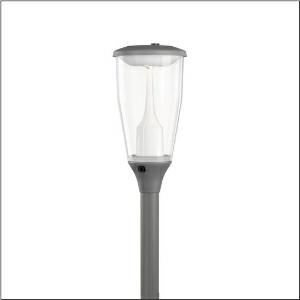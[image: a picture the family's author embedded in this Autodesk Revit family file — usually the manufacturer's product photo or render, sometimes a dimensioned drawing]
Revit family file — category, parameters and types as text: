
# Revit family: dl_11_iq___st1_2a_5xa5575ew14hp00022_a9c4
name_source: partatom
category: Lighting Fixtures
units: mm (PartAtom-declared; Revit-internal decimal feet)

## family parameters
Cut with Voids When Loaded = No
Host = Face
Light Source = No
Part Type = Normal
Room Calculation Point = No
Round Connector Dimension = Use Diameter
Shared = No

## types (1)
- --- (1 x LED, 4790 lm, 33.5 W, 3000K)
    Apparent Load = 34 VA
    CIE Flux Codes = 23 60 93 95 100
    Color Rendering = 70
    Color Temperature = 3000K
    Default Elevation = 1800 mm
    Description = DL 11 iQ, mast luminaire, Module 540 iQ-SR, primary light control with 3 zone facetted reflector, of plastic, silver coated, highly specular, structured, primary optical cover: cover, of PMMA, transparent, light distribution: ST1.2a, light emission: direct distribution, primary light characteristic: asymmetric, installation type: post-top, LED, High Power LED, rated luminous flux: 4.790lm, luminous efficacy: 143lm/W, light colour: 730, colour temperature: 3000K, control gear: iQ-Street Remote, D4i with power reduction, control: pre-setting: logarithmic dimming characteristic, Street-Remote, Auto-Match, Temp-Guard, Lumen-Switch, Night-Set, Smart-Wire, Light-Fading, Desk-Remote (wireless, voltage-free reading and setting of iQ features in the workshop via application-optimized NFC function/RFID function), optimised constant luminous flux control (CLO 2.0), mains connection: 220..240V, AC, 50/60Hz, connection cable pre-assembled, cable length: 5,5m, start of lifetime: 34W, end of service life: 36W, reduction: 15W, luminaire housing, upper part, of diecast aluminium, coated, SITECO metallic grey (DB 702S), spigot size: 76mm (post-top), mounting height: 3..5m, post-top mast mounting element, of diecast aluminium, coated, SITECO metallic grey (DB 702S), Module 540 iQ-SR, traffic white (RAL 9016), equipment: Power, Smart Interface above and design motion detector below, protection rating (complete): IP65, insulation class (complete): insulation class II (safety insulation), certification: CE, ENEC, ENEC+, VDE, impact resistance: IK07, packaging unit: 1 piece

Light Distribution: ST1.2a
    Height = 665 mm
    Lamp = 1 x LED
    Lamp Light Flux = 4790 lm
    Lamp Power = 33.5 W
    Lamp count = 1
    Length = 334 mm
    Luminous efficacy = 143 lm/W
    Manufacturer = Siteco
    ModVariant = No
    Model = 5XA5575EW14HP00022
    Number of Poles = 1
    OnlyDefault = Yes
    Power Factor = 1
    Product Name = DL 11 iQ | ST1.2a
    Product group = mast luminaire | pylon top
    ProductGroupID = 6100
    Protection Class = Protection class II
    Protection Degree = IP 65
    RLX_Detail_Level = 1
    RLX_Emergency_Light_Flux = 0 lm
    RLX_Emergency_Type = 0
    RLX_Emergency_Type_DB = No
    RlxData = <blob elided: 161385 chars, md5=24dc3fef>
    Socket = socket
    Standby Power = 0 W
    System Light Flux = 4790 lm
    System Power = 34 W
    Type Comments = factory setting: luminous flux: 100 % | dim-lin: 254 | 695 mA
    Type Image = l_1337543.jpg
    URL = http://relux.com
    VarID = @adj_040387
    Voltage = 0 V
    Weight = 0.00 kg
    Width = 0 mm  [stored 0 ft]

note: [stored X ft] marks values corroborated as IEEE doubles in the binary element streams (Revit-internal decimal feet)

## geometry (parser evidence)
native form markers: Blend x4, Sweep x12
no freeform markers — native parametric forms only
